FCSTD DOCUMENT  (FreeCAD 1.0R39285 (Git))
Label: enclosure
License: All rights reserved
LicenseURL: https://en.wikipedia.org/wiki/All_rights_reserved
objects: Sketcher::SketchObject×2, PartDesign::Body×1
note: 5 computed .brp shape members not serialized (recipe doc carries the construction recipe); baked Part::Feature solids carry a one-line shape summary decoded from their .brp

FEATURE [Sketcher::SketchObject] Sketch  label="Edge_Cuts"
  ArcFitTolerance = 1e-06
  AttachmentSupport = -> [XY_Plane]
  FullyConstrained = true
  MakeInternals = false
  MapMode = 5
  sketch-geometry (28):
    g0: LineSegment StartX=-7.75 StartY=36 StartZ=0 EndX=7.75 EndY=36 EndZ=0
    g1: ArcOfCircle CenterX=7.75 CenterY=32 CenterZ=0 NormalX=0 NormalY=0 NormalZ=1 AngleXU=0 Radius=4 StartAngle=0.678382 EndAngle=1.5708
    g2: LineSegment StartX=10.8644 StartY=34.5101 StartZ=0 EndX=18.0073 EndY=25.6478 EndZ=0
    g3: ArcOfCircle CenterX=11 CenterY=20 CenterZ=0 NormalX=0 NormalY=0 NormalZ=1 AngleXU=0 Radius=9 StartAngle=-4.88e-14 EndAngle=0.678382
    g4: LineSegment StartX=20 StartY=20 StartZ=0 EndX=20 EndY=-20 EndZ=0
    g5: ArcOfCircle CenterX=16 CenterY=-20 CenterZ=0 NormalX=0 NormalY=0 NormalZ=1 AngleXU=0 Radius=4 StartAngle=4.71239 EndAngle=6.28319
    g6: LineSegment StartX=16 StartY=-24 StartZ=0 EndX=-16 EndY=-24 EndZ=0
    g7: ArcOfCircle CenterX=-16 CenterY=-20 CenterZ=0 NormalX=0 NormalY=0 NormalZ=1 AngleXU=0 Radius=4 StartAngle=3.14159 EndAngle=4.71239
    g8: LineSegment StartX=-20 StartY=-20 StartZ=0 EndX=-20 EndY=20 EndZ=0
    g9: ArcOfCircle CenterX=-11 CenterY=20 CenterZ=0 NormalX=0 NormalY=0 NormalZ=1 AngleXU=0 Radius=9 StartAngle=2.46321 EndAngle=3.14159
    g10: LineSegment StartX=-18.0073 StartY=25.6478 StartZ=0 EndX=-10.8644 EndY=34.5101 EndZ=0
    g11: ArcOfCircle CenterX=-7.75 CenterY=32 CenterZ=0 NormalX=0 NormalY=0 NormalZ=1 AngleXU=0 Radius=4 StartAngle=1.5708 EndAngle=2.46321
    g12: GeomPoint X=0 Y=36 Z=0
    g13: LineSegment [constr] StartX=-20 StartY=0 StartZ=0 EndX=20 EndY=0 EndZ=0
    g14: GeomPoint [constr] X=0 Y=0 Z=0
    g15: LineSegment [constr] StartX=4e-16 StartY=36 StartZ=0 EndX=4e-16 EndY=-24 EndZ=0
    g16: Circle CenterX=7.75 CenterY=32 CenterZ=0 NormalX=0 NormalY=0 NormalZ=1 AngleXU=0 Radius=1.6
    g17: Circle CenterX=-7.75 CenterY=32 CenterZ=0 NormalX=0 NormalY=0 NormalZ=1 AngleXU=0 Radius=1.6
    g18: Circle CenterX=-16 CenterY=-20 CenterZ=0 NormalX=0 NormalY=0 NormalZ=1 AngleXU=0 Radius=1.6
    g19: Circle CenterX=16 CenterY=-20 CenterZ=0 NormalX=0 NormalY=0 NormalZ=1 AngleXU=0 Radius=1.6
    g20: Circle [constr] CenterX=7.75 CenterY=32 CenterZ=0 NormalX=0 NormalY=0 NormalZ=1 AngleXU=0 Radius=2.75
    g21: Circle [constr] CenterX=-7.75 CenterY=32 CenterZ=0 NormalX=0 NormalY=0 NormalZ=1 AngleXU=0 Radius=2.75
    g22: Circle [constr] CenterX=16 CenterY=-20 CenterZ=0 NormalX=0 NormalY=0 NormalZ=1 AngleXU=0 Radius=2.75
    g23: Circle [constr] CenterX=-16 CenterY=-20 CenterZ=0 NormalX=0 NormalY=0 NormalZ=1 AngleXU=0 Radius=2.75
    g24: LineSegment [constr] StartX=-5 StartY=32 StartZ=0 EndX=5 EndY=32 EndZ=0
    g25: GeomPoint [constr] X=-20 Y=9e-16 Z=0
    g26: GeomPoint [constr] X=-20 Y=7e-16 Z=0
    g27: GeomPoint [constr] X=20 Y=-9e-16 Z=0
  constraints (60):
    c: Horizontal(g0)
    c: Tangent(g0,g1) = 1.5708
    c: Tangent(g1,g2) = 1.5708
    c: Tangent(g2,g3) = 1.5708
    c: Tangent(g3,g4) = 1.5708
    c: Tangent(g4,g5) = 1.5708
    c: Tangent(g5,g6) = 1.5708
    c: Tangent(g6,g7) = 1.5708
    c: Tangent(g7,g8) = 1.5708
    c: Tangent(g8,g9) = 1.5708
    c: Tangent(g9,g10) = 1.5708
    c: Tangent(g10,g11) = 1.5708
    c: Tangent(g11,g0) = 1.5708
    c: Vertical(g8)
    c: Vertical(g4)
    c: Horizontal(g6)
    c: Symmetric(g0,g0,g12)
    c: PointOnObject(g12,g-2)
    c: Symmetric(g8,g8,g13)
    c: Symmetric(g4,g4,g13)
    c: Horizontal(g13)
    c: Symmetric(g13,g13,g14)
    c: PointOnObject(g14,g-2)
    c: Equal(g11,g1)
    c: DistanceX(g13,g13) = 40
    c: Symmetric(g0,g0,g15)
    c: PointOnObject(g15,g6)
    c: Vertical(g15)
    c: Equal(g9,g3)
    c: Equal(g10,g2)
    c: DistanceY(g15,g15) = 60
    c: Radius(g5) = 4
    c: Equal(g11,g7)
    c: Coincident(g16,g1)
    c: Diameter(g16) = 3.2
    c: Coincident(g17,g11)
    c: Coincident(g18,g7)
    c: Coincident(g19,g5)
    c: Equal(g18,g19)
    c: Equal(g19,g17)
    c: Equal(g17,g16)
    c: Coincident(g20,g1)
    c: Diameter(g20) = 5.5
    c: Coincident(g21,g11)
    c: Coincident(g22,g5)
    c: Coincident(g23,g7)
    c: Equal(g21,g23)
    c: Equal(g23,g22)
    c: Equal(g22,g20)
    c: PointOnObject(g24,g21)
    c: PointOnObject(g24,g20)
    c: Horizontal(g24)
    c: DistanceX(g24,g24) = 10
    c: Symmetric(g8,g8,g25)
    c: Symmetric(g8,g8,g26)
    c: DistanceY(g4,g4) = 40
    c: Symmetric(g4,g4,g27)
    c: Perpendicular(g21,g24)
    c: Radius(g3) = 9
    c: PointOnObject(g13,g-1)
FEATURE [Sketcher::SketchObject] Sketch001  label="References"
  ArcFitTolerance = 1e-06
  AttachmentSupport = -> [XY_Plane]
  FullyConstrained = true
  MakeInternals = false
  MapMode = 5
  sketch-geometry (28):
    g0: LineSegment StartX=-7.75 StartY=36 StartZ=0 EndX=7.75 EndY=36 EndZ=0
    g1: ArcOfCircle CenterX=7.75 CenterY=32 CenterZ=0 NormalX=0 NormalY=0 NormalZ=1 AngleXU=0 Radius=4 StartAngle=0.678382 EndAngle=1.5708
    g2: LineSegment StartX=10.8644 StartY=34.5101 StartZ=0 EndX=18.0073 EndY=25.6478 EndZ=0
    g3: ArcOfCircle CenterX=11 CenterY=20 CenterZ=0 NormalX=0 NormalY=0 NormalZ=1 AngleXU=0 Radius=9 StartAngle=-4.88e-14 EndAngle=0.678382
    g4: LineSegment StartX=20 StartY=20 StartZ=0 EndX=20 EndY=-20 EndZ=0
    g5: ArcOfCircle CenterX=16 CenterY=-20 CenterZ=0 NormalX=0 NormalY=0 NormalZ=1 AngleXU=0 Radius=4 StartAngle=4.71239 EndAngle=6.28319
    g6: LineSegment StartX=16 StartY=-24 StartZ=0 EndX=-16 EndY=-24 EndZ=0
    g7: ArcOfCircle CenterX=-16 CenterY=-20 CenterZ=0 NormalX=0 NormalY=0 NormalZ=1 AngleXU=0 Radius=4 StartAngle=3.14159 EndAngle=4.71239
    g8: LineSegment StartX=-20 StartY=-20 StartZ=0 EndX=-20 EndY=20 EndZ=0
    g9: ArcOfCircle CenterX=-11 CenterY=20 CenterZ=0 NormalX=0 NormalY=0 NormalZ=1 AngleXU=0 Radius=9 StartAngle=2.46321 EndAngle=3.14159
    g10: LineSegment StartX=-18.0073 StartY=25.6478 StartZ=0 EndX=-10.8644 EndY=34.5101 EndZ=0
    g11: ArcOfCircle CenterX=-7.75 CenterY=32 CenterZ=0 NormalX=0 NormalY=0 NormalZ=1 AngleXU=0 Radius=4 StartAngle=1.5708 EndAngle=2.46321
    g12: GeomPoint X=0 Y=36 Z=0
    g13: LineSegment StartX=-20 StartY=0 StartZ=0 EndX=20 EndY=0 EndZ=0
    g14: GeomPoint [constr] X=0 Y=0 Z=0
    g15: LineSegment StartX=4e-16 StartY=36 StartZ=0 EndX=4e-16 EndY=-24 EndZ=0
    g16: Circle CenterX=7.75 CenterY=32 CenterZ=0 NormalX=0 NormalY=0 NormalZ=1 AngleXU=0 Radius=1.6
    g17: Circle CenterX=-7.75 CenterY=32 CenterZ=0 NormalX=0 NormalY=0 NormalZ=1 AngleXU=0 Radius=1.6
    g18: Circle CenterX=-16 CenterY=-20 CenterZ=0 NormalX=0 NormalY=0 NormalZ=1 AngleXU=0 Radius=1.6
    g19: Circle CenterX=16 CenterY=-20 CenterZ=0 NormalX=0 NormalY=0 NormalZ=1 AngleXU=0 Radius=1.6
    g20: Circle CenterX=7.75 CenterY=32 CenterZ=0 NormalX=0 NormalY=0 NormalZ=1 AngleXU=0 Radius=2.75
    g21: Circle CenterX=-7.75 CenterY=32 CenterZ=0 NormalX=0 NormalY=0 NormalZ=1 AngleXU=0 Radius=2.75
    g22: Circle CenterX=16 CenterY=-20 CenterZ=0 NormalX=0 NormalY=0 NormalZ=1 AngleXU=0 Radius=2.75
    g23: Circle CenterX=-16 CenterY=-20 CenterZ=0 NormalX=0 NormalY=0 NormalZ=1 AngleXU=0 Radius=2.75
    g24: LineSegment [constr] StartX=-5 StartY=32 StartZ=0 EndX=5 EndY=32 EndZ=0
    g25: GeomPoint [constr] X=-20 Y=9e-16 Z=0
    g26: GeomPoint [constr] X=-20 Y=7e-16 Z=0
    g27: GeomPoint [constr] X=20 Y=-9e-16 Z=0
  constraints (60):
    c: Horizontal(g0)
    c: Tangent(g0,g1) = 1.5708
    c: Tangent(g1,g2) = 1.5708
    c: Tangent(g2,g3) = 1.5708
    c: Tangent(g3,g4) = 1.5708
    c: Tangent(g4,g5) = 1.5708
    c: Tangent(g5,g6) = 1.5708
    c: Tangent(g6,g7) = 1.5708
    c: Tangent(g7,g8) = 1.5708
    c: Tangent(g8,g9) = 1.5708
    c: Tangent(g9,g10) = 1.5708
    c: Tangent(g10,g11) = 1.5708
    c: Tangent(g11,g0) = 1.5708
    c: Vertical(g8)
    c: Vertical(g4)
    c: Horizontal(g6)
    c: Symmetric(g0,g0,g12)
    c: PointOnObject(g12,g-2)
    c: Symmetric(g8,g8,g13)
    c: Symmetric(g4,g4,g13)
    c: Horizontal(g13)
    c: Symmetric(g13,g13,g14)
    c: PointOnObject(g14,g-2)
    c: Equal(g11,g1)
    c: DistanceX(g13,g13) = 40
    c: Symmetric(g0,g0,g15)
    c: PointOnObject(g15,g6)
    c: Vertical(g15)
    c: Equal(g9,g3)
    c: Equal(g10,g2)
    c: DistanceY(g15,g15) = 60
    c: Radius(g5) = 4
    c: Equal(g11,g7)
    c: Coincident(g16,g1)
    c: Diameter(g16) = 3.2
    c: Coincident(g17,g11)
    c: Coincident(g18,g7)
    c: Coincident(g19,g5)
    c: Equal(g18,g19)
    c: Equal(g19,g17)
    c: Equal(g17,g16)
    c: Coincident(g20,g1)
    c: Diameter(g20) = 5.5
    c: Coincident(g21,g11)
    c: Coincident(g22,g5)
    c: Coincident(g23,g7)
    c: Equal(g21,g23)
    c: Equal(g23,g22)
    c: Equal(g22,g20)
    c: PointOnObject(g24,g21)
    c: PointOnObject(g24,g20)
    c: Horizontal(g24)
    c: DistanceX(g24,g24) = 10
    c: Symmetric(g8,g8,g25)
    c: Symmetric(g8,g8,g26)
    c: DistanceY(g4,g4) = 40
    c: Symmetric(g4,g4,g27)
    c: Perpendicular(g21,g24)
    c: Radius(g3) = 9
    c: PointOnObject(g13,g-1)
FEATURE [PartDesign::Body] Body  label="Board_Outline"
  AllowCompound = false
  Group = -> [Sketch,Sketch001]
  Origin = -> Origin
